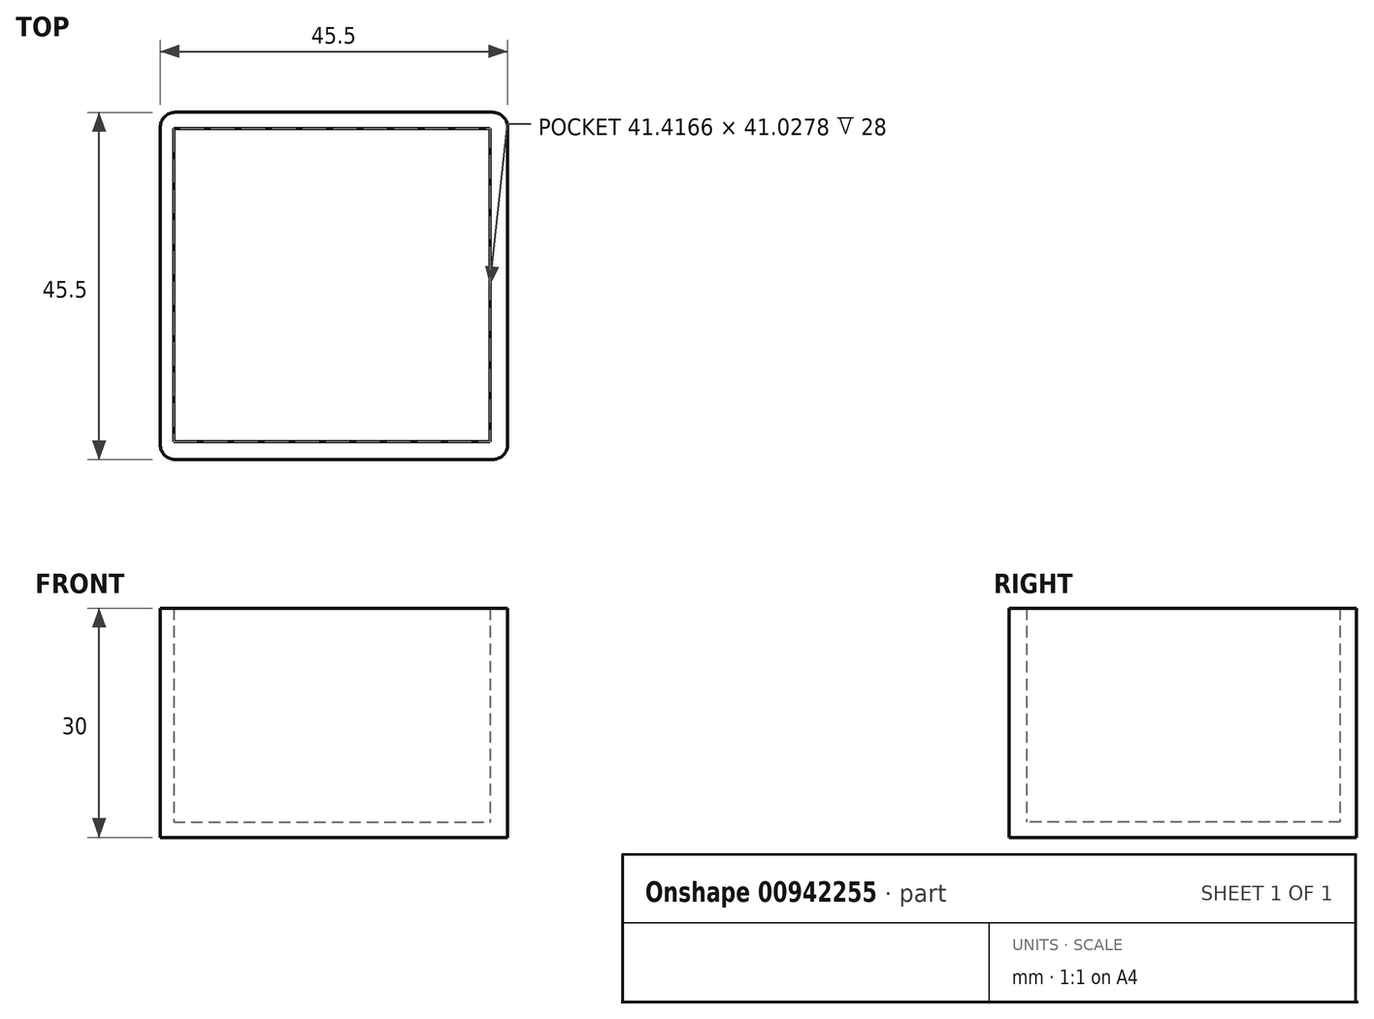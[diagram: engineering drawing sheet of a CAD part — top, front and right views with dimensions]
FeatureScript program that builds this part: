
annotation { "Feature Type Name" : "Feature", "Feature Type Description" : "" }
export const myFeature = defineFeature(function(context is Context, id is Id, definition is map)
    precondition{}
    {
        {
            var Q0;
            Q0=qCreatedBy(makeId("Top.planeOp"),FACE);
            var sketch = newSketch(context, id + "F0", { "sketchPlane" : qUnion([Q0])});
            skLineSegment(sketch, "E0.bottom", {"start": v(20.7, -20.51) * mm, "end": v(-20.7, -20.51) * mm});
            skLineSegment(sketch, "E0.top", {"start": v(20.7, 20.51) * mm, "end": v(-20.7, 20.51) * mm});
            skLineSegment(sketch, "E0.left", {"start": v(20.7, -20.51) * mm, "end": v(20.7, 20.51) * mm});
            skLineSegment(sketch, "E0.right", {"start": v(-20.7, -20.51) * mm, "end": v(-20.7, 20.51) * mm});
            skPoint(sketch, "E0.middle", {"position": v(0, 0) * mm});
            skLineSegment(sketch, "E1.bottom", {"start": v(23.04, -22.85) * mm, "end": v(-22.46, -22.85) * mm});
            skLineSegment(sketch, "E1.top", {"start": v(23.04, 22.65) * mm, "end": v(-22.46, 22.65) * mm});
            skLineSegment(sketch, "E1.left", {"start": v(23.04, -22.85) * mm, "end": v(23.04, 22.65) * mm});
            skLineSegment(sketch, "E1.right", {"start": v(-22.46, -22.85) * mm, "end": v(-22.46, 22.65) * mm});
            skPoint(sketch, "E1.middle", {"position": v(0.3, -0.1) * mm});
            skSolve(sketch);
        }
        {
            var Q0;
            Q0=makeQuery(id+"F0.imprint","IMPRINT",FACE,{"disambiguationData":[TD([[makeQuery(id+"F0.imprint","IMPRINT",EDGE,{"derivedFrom":sQuery(id+"F0.wireOp",EDGE,"E0.bottom")}),1.0]])]});
            var Q1;
            Q1=makeQuery(id+"F0.imprint","IMPRINT",FACE,{"disambiguationData":[TD([[makeQuery(id+"F0.imprint","IMPRINT",EDGE,{"derivedFrom":sQuery(id+"F0.wireOp",EDGE,"E0.bottom")}),-1.0]])]});
            extrude(context, id + "F1", {"entities" : qUnion([Q0, Q1]), "depth" : 2 * mm, "offsetDistance" : 25 * mm});
        }
        {
            var Q0;
            Q0=makeQuery(id+"F0.imprint","IMPRINT",FACE,{"disambiguationData":[TD([[makeQuery(id+"F0.imprint","IMPRINT",EDGE,{"derivedFrom":sQuery(id+"F0.wireOp",EDGE,"E0.bottom")}),1.0]])]});
            extrude(context, id + "F2", {"entities" : qUnion([Q0]), "operationType" : NewBodyOperationType.ADD, "depth" : 30 * mm, "offsetDistance" : 25 * mm});
        }
        {
            var Q0;
            {var subQ0=sQuery(id+"F0.wireOp",EDGE,"E1.right");var subQ1=sQuery(id+"F0.wireOp",EDGE,"E1.bottom");Q0=makeQuery(id+"F2.boolean.opBoolean","MERGE",EDGE,{"derivedFrom":[makeQuery(id+"F1.opExtrude","SWEPT_EDGE",EDGE,{"disambiguationData":[OSD([subQ1,subQ0])]}),makeQuery(id+"F2.opExtrude","SWEPT_EDGE",EDGE,{"disambiguationData":[OSD([subQ1,subQ0])]})]});}
            var Q1;
            {var subQ0=sQuery(id+"F0.wireOp",EDGE,"E1.left");var subQ1=sQuery(id+"F0.wireOp",EDGE,"E1.bottom");Q1=makeQuery(id+"F2.boolean.opBoolean","MERGE",EDGE,{"derivedFrom":[makeQuery(id+"F1.opExtrude","SWEPT_EDGE",EDGE,{"disambiguationData":[OSD([subQ1,subQ0])]}),makeQuery(id+"F2.opExtrude","SWEPT_EDGE",EDGE,{"disambiguationData":[OSD([subQ1,subQ0])]})]});}
            var Q2;
            {var subQ0=sQuery(id+"F0.wireOp",EDGE,"E1.left");var subQ1=sQuery(id+"F0.wireOp",EDGE,"E1.top");Q2=makeQuery(id+"F2.boolean.opBoolean","MERGE",EDGE,{"derivedFrom":[makeQuery(id+"F1.opExtrude","SWEPT_EDGE",EDGE,{"disambiguationData":[OSD([subQ1,subQ0])]}),makeQuery(id+"F2.opExtrude","SWEPT_EDGE",EDGE,{"disambiguationData":[OSD([subQ1,subQ0])]})]});}
            var Q3;
            {var subQ0=sQuery(id+"F0.wireOp",EDGE,"E1.right");var subQ1=sQuery(id+"F0.wireOp",EDGE,"E1.top");Q3=makeQuery(id+"F2.boolean.opBoolean","MERGE",EDGE,{"derivedFrom":[makeQuery(id+"F1.opExtrude","SWEPT_EDGE",EDGE,{"disambiguationData":[OSD([subQ1,subQ0])]}),makeQuery(id+"F2.opExtrude","SWEPT_EDGE",EDGE,{"disambiguationData":[OSD([subQ1,subQ0])]})]});}
            fillet(context, id + "F3", {"entities" : qUnion([Q0, Q1, Q2, Q3]), "radius" : 2 * mm, "tangentPropagation" : true, "allowEdgeOverflow" : false});
        }
    });
